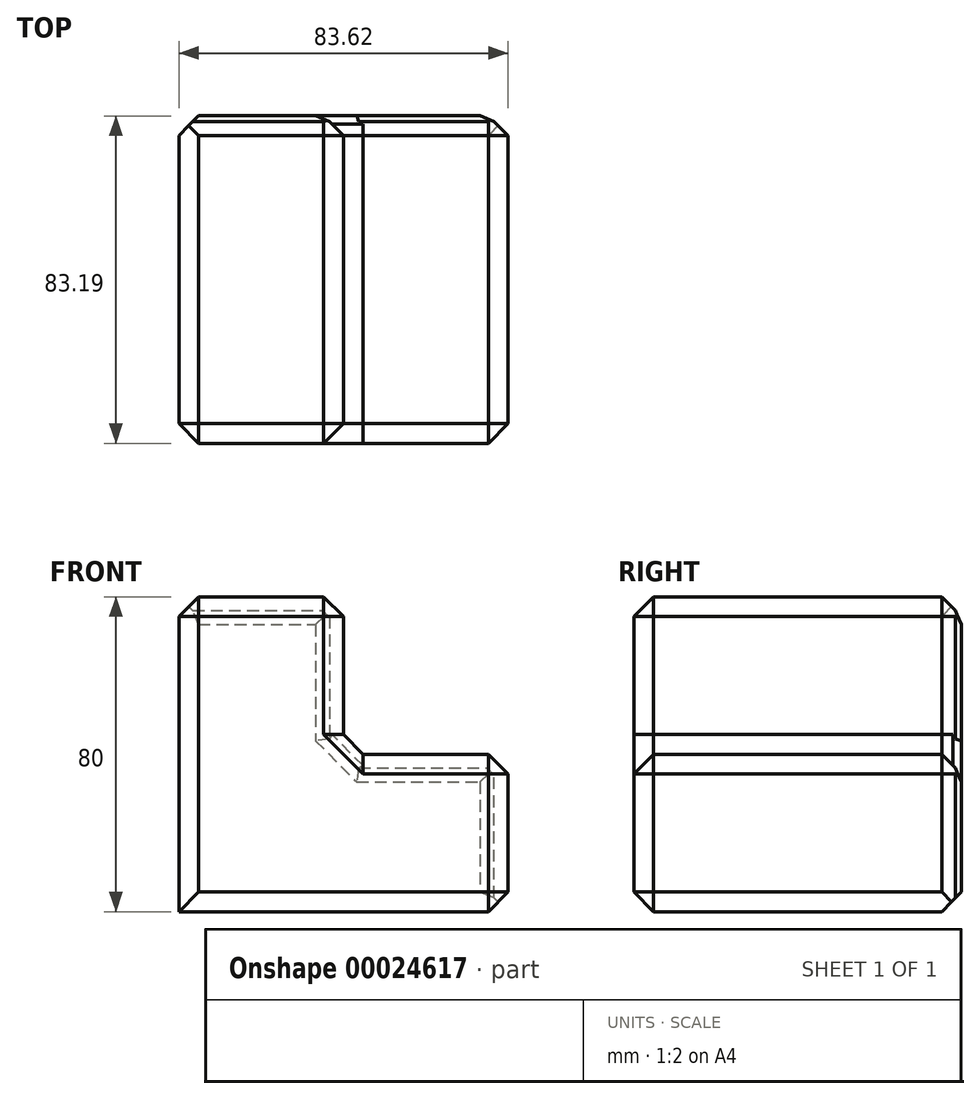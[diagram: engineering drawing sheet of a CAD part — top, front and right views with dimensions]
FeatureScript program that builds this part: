
annotation { "Feature Type Name" : "Feature", "Feature Type Description" : "" }
export const myFeature = defineFeature(function(context is Context, id is Id, definition is map)
    precondition{}
    {
        {
            var Q0;
            Q0=qCreatedBy(makeId("Top.planeOp"),FACE);
            var sketch = newSketch(context, id + "F0", { "sketchPlane" : qUnion([Q0])});
            skLineSegment(sketch, "E0.bottom", {"start": v(-59.13, -45.93) * mm, "end": v(24.5, -45.93) * mm});
            skLineSegment(sketch, "E0.top", {"start": v(-59.13, 37.26) * mm, "end": v(24.5, 37.26) * mm});
            skLineSegment(sketch, "E0.left", {"start": v(-59.13, -45.93) * mm, "end": v(-59.13, 37.26) * mm});
            skLineSegment(sketch, "E0.right", {"start": v(24.5, -45.93) * mm, "end": v(24.5, 37.26) * mm});
            skSolve(sketch);
        }
        {
            var Q0;
            Q0=makeQuery(id+"F0.imprint","IMPRINT",FACE,{"disambiguationData":[TD([[makeQuery(id+"F0.imprint","IMPRINT",EDGE,{"derivedFrom":sQuery(id+"F0.wireOp",EDGE,"E0.bottom")}),1.0]])]});
            extrude(context, id + "F1", {"entities" : qUnion([Q0]), "depth" : 40 * mm});
        }
        {
            var Q0;
            Q0=makeQuery(id+"F1.opExtrude","CAP_FACE",FACE,{"disambiguationData":[OSD([sQuery(id+"F0.wireOp",EDGE,"E0.bottom"),sQuery(id+"F0.wireOp",EDGE,"E0.top"),sQuery(id+"F0.wireOp",EDGE,"E0.left"),sQuery(id+"F0.wireOp",EDGE,"E0.right")])],"isStart":false});
            var sketch = newSketch(context, id + "F2", { "sketchPlane" : qUnion([Q0])});
            skLineSegment(sketch, "E1", {"start": v(-17.32, 37.26) * mm, "end": v(-17.32, -45.93) * mm});
            skSolve(sketch);
        }
        {
            var Q0;
            {var subQ1=sQuery(id+"F2.wireOp",EDGE,"E1");Q0=makeQuery(id+"F2.imprint","IMPRINT",FACE,{"disambiguationData":[TD([[makeQuery(id+"F2.imprint","IMPRINT",EDGE,{"derivedFrom":subQ1}),-1.0]])]});}
            extrude(context, id + "F3", {"entities" : qUnion([Q0]), "operationType" : NewBodyOperationType.ADD, "depth" : 40 * mm});
        }
        {
            var Q0;
            Q0=makeQuery(id+"F3.opExtrude","CAP_FACE",FACE,{"disambiguationData":[OSD([sQuery(id+"F0.wireOp",EDGE,"E0.bottom"),sQuery(id+"F0.wireOp",EDGE,"E0.top"),sQuery(id+"F0.wireOp",EDGE,"E0.left"),sQuery(id+"F2.wireOp",EDGE,"E1")])],"isStart":false});
            var Q1;
            Q1=makeQuery(id+"F3.opExtrude","SWEPT_FACE",FACE,{"disambiguationData":[OSD([sQuery(id+"F2.wireOp",EDGE,"E1")])]});
            var Q2;
            {var subQ0=sQuery(id+"F0.wireOp",EDGE,"E0.bottom");Q2=makeQuery(id+"F3.boolean.opBoolean","MERGE",FACE,{"derivedFrom":[makeQuery(id+"F1.opExtrude","SWEPT_FACE",FACE,{"disambiguationData":[OSD([subQ0])]}),makeQuery(id+"F3.opExtrude","SWEPT_FACE",FACE,{"disambiguationData":[OSD([subQ0])]})]});}
            var Q3;
            Q3=makeQuery(id+"F1.opExtrude","CAP_FACE",FACE,{"disambiguationData":[OSD([sQuery(id+"F0.wireOp",EDGE,"E0.bottom"),sQuery(id+"F0.wireOp",EDGE,"E0.top"),sQuery(id+"F0.wireOp",EDGE,"E0.left"),sQuery(id+"F0.wireOp",EDGE,"E0.right")])],"isStart":false});
            var Q4;
            Q4=makeQuery(id+"F1.opExtrude","SWEPT_FACE",FACE,{"disambiguationData":[OSD([sQuery(id+"F0.wireOp",EDGE,"E0.right")])]});
            chamfer(context, id + "F4", {"entities" : qUnion([Q0, Q1, Q2, Q3, Q4]), "width" : 5 * mm, "tangentPropagation" : true});
        }
        {
            var Q0;
            {var subQ0=sQuery(id+"F0.wireOp",EDGE,"E0.top");Q0=makeQuery(id+"F3.boolean.opBoolean","MERGE",FACE,{"derivedFrom":[makeQuery(id+"F1.opExtrude","SWEPT_FACE",FACE,{"disambiguationData":[OSD([subQ0])]}),makeQuery(id+"F3.opExtrude","SWEPT_FACE",FACE,{"disambiguationData":[OSD([subQ0])]})]});}
            chamfer(context, id + "F5", {"entities" : qUnion([Q0]), "width" : 5 * mm, "tangentPropagation" : true});
        }
    });
